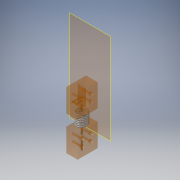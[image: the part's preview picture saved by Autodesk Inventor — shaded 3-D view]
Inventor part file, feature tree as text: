
AUTODESK INVENTOR PART (.ipt)
format: ipt  version: 2016 (Build 200138000, 138)  size: 534,016 bytes
history: native  units: in
note: dims shown in document units (in); Inventor stores cm internally (conversion verified against a paired STEP export)
features: reference x2, surface_op x2, other x2, plane x1, helix x1, sketch x1
ambient origin geometry x8: Origin, YZ Plane, XZ Plane, XY Plane, X Axis, Y Axis, Z Axis, Center Point
bodies: Solid1 (feature_tree)
feature tree (9):
  plane  "Work Plane1"
  helix  "Coil1"  [1 undecoded]
  sketch  "Sketch1"  dims[d1=0.08in d2=1.0in d3=1.0in d4=0.92in d5=2.7559in d6=0.0in d7=90.0deg d8=90.0deg d9=0.0in d10=0.0in]
  reference  "Reference1"
  reference  "Reference2"
  surface_op  "Surface1"
  surface_op  "Surface2"
  other  "Srf1"
  other  "Srf2"
note: 1 required parameter value undecoded (feature->parameter linkage not recoverable at this tier; creation-order binding heuristic only, values carry confidence <= 0.55)
